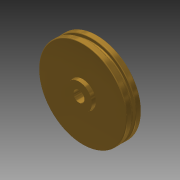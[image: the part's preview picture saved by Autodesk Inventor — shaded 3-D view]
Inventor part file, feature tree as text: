
AUTODESK INVENTOR PART (.ipt)
format: ipt  version: 2015 SP1 (Build 190203100, 203)  size: 183,808 bytes
history: native  units: in
note: dims shown in document units (in); Inventor stores cm internally (conversion verified against a paired STEP export)
features: extrude x4, sketch x4, plane x1, fillet x1, projected_geometry x1
ambient origin geometry x8: Origin, YZ Plane, XZ Plane, XY Plane, X Axis, Y Axis, Z Axis, Center Point
bodies: Solid1 (feature_tree)
feature tree (11):
  extrude  "Extrusion1"  Depth=3.0in
  plane  "Work Plane1"
  extrude  "Extrusion3"  Depth=0.5in
  extrude  "Extrusion4"  Depth=0.75in
  extrude  "Extrusion5"  Depth=0.125in
  fillet  "Fillet2"  [1 undecoded]
  sketch  "Sketch1"  dims[d0=0.9in d1=3.0in]
  sketch  "Sketch3"  dims[d2=0.5in d3=0.0in d9=0.875in]
  sketch  "Sketch4"  dims[d10=0.75in d11=0.0in d12=0.375in]
  sketch  "Sketch5"  dims[d13=1.0in d14=0.0in d15=0.125in d16=0.0in d17=0.125in d18=0.0in d19=0.0312in]
  projected_geometry  "Projected Loop1"
note: 1 required parameter value undecoded (feature->parameter linkage not recoverable at this tier; creation-order binding heuristic only, values carry confidence <= 0.55)
